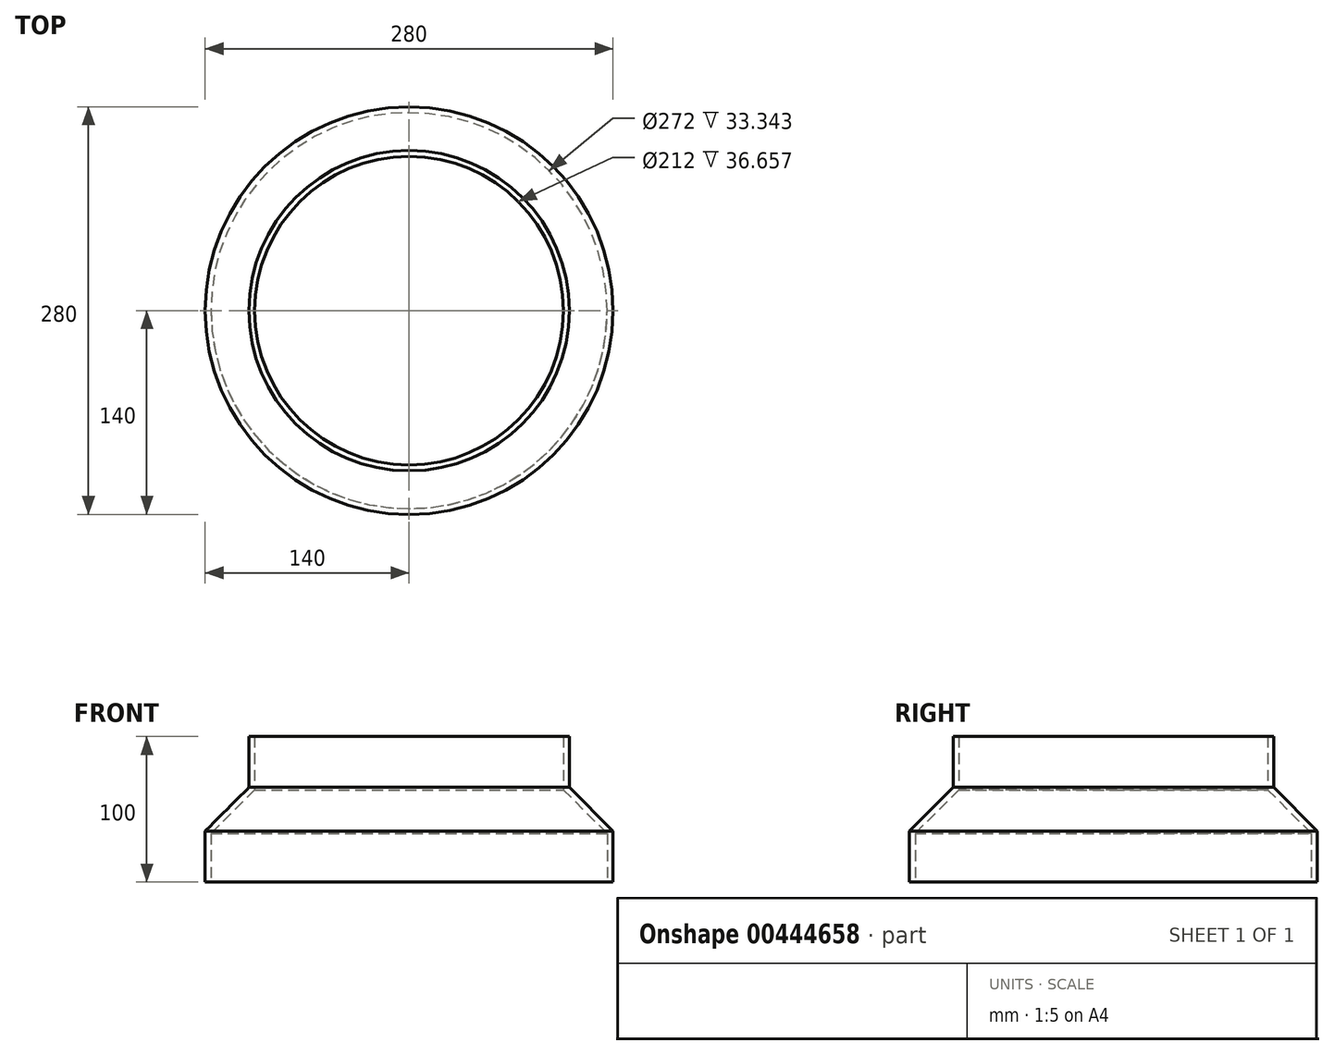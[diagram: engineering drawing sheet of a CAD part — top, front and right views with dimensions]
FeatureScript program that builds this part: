
annotation { "Feature Type Name" : "Feature", "Feature Type Description" : "" }
export const myFeature = defineFeature(function(context is Context, id is Id, definition is map)
    precondition{}
    {
        {
            var Q0;
            Q0=qCreatedBy(makeId("Front.planeOp"),FACE);
            var sketch = newSketch(context, id + "F0", { "sketchPlane" : qUnion([Q0])});
            skLineSegment(sketch, "E0", {"start": v(-140, 0) * mm, "end": v(-140, 35) * mm});
            skLineSegment(sketch, "E1", {"start": v(-140, 35) * mm, "end": v(-110, 65) * mm});
            skLineSegment(sketch, "E2", {"start": v(-110, 65) * mm, "end": v(-110, 100) * mm});
            skLineSegment(sketch, "E3", {"start": v(-140, 0) * mm, "end": v(0, 0) * mm});
            skLineSegment(sketch, "E4", {"start": v(0, 0) * mm, "end": v(0, 100) * mm});
            skLineSegment(sketch, "E5", {"start": v(0, 100) * mm, "end": v(-110, 100) * mm});
            skSolve(sketch);
        }
        {
            var Q0;
            Q0=makeQuery(id+"F0.imprint","IMPRINT",FACE,{"disambiguationData":[TD([[makeQuery(id+"F0.imprint","IMPRINT",EDGE,{"derivedFrom":sQuery(id+"F0.wireOp",EDGE,"E0")}),-1.0]])]});
            var Q1;
            Q1=sQuery(id+"F0.wireOp",EDGE,"E4");
            revolve(context, id + "F1", {"entities" : qUnion([Q0]), "axis" : qUnion([Q1]), "revolveType" : RevolveType.FULL});
        }
        {
            var Q0;
            Q0=makeQuery(id+"F1.opRevolve","SWEPT_FACE",FACE,{"disambiguationData":[OSD([sQuery(id+"F0.wireOp",EDGE,"E3")])]});
            shell(context, id + "F2", {"entities" : qUnion([Q0]), "thickness" : 4 * mm});
        }
        {
            var Q0;
            Q0=makeQuery(id+"F1.opRevolve","SWEPT_FACE",FACE,{"disambiguationData":[OSD([sQuery(id+"F0.wireOp",EDGE,"E5")])]});
            var sketch = newSketch(context, id + "F3", { "sketchPlane" : qUnion([Q0])});
            skCircle(sketch, "E6", {"center": v(0, 0) * mm, "radius": 106 * mm});
            skSolve(sketch);
        }
        {
            var Q0;
            Q0=makeQuery(id+"F3.imprint","IMPRINT",FACE,{"disambiguationData":[TD([[makeQuery(id+"F3.imprint","IMPRINT",EDGE,{"derivedFrom":sQuery(id+"F3.wireOp",EDGE,"E6")}),1.0]])]});
            extrude(context, id + "F4", {"entities" : qUnion([Q0]), "operationType" : NewBodyOperationType.REMOVE, "oppositeDirection" : true, "depth" : 25 * mm});
        }
    });
